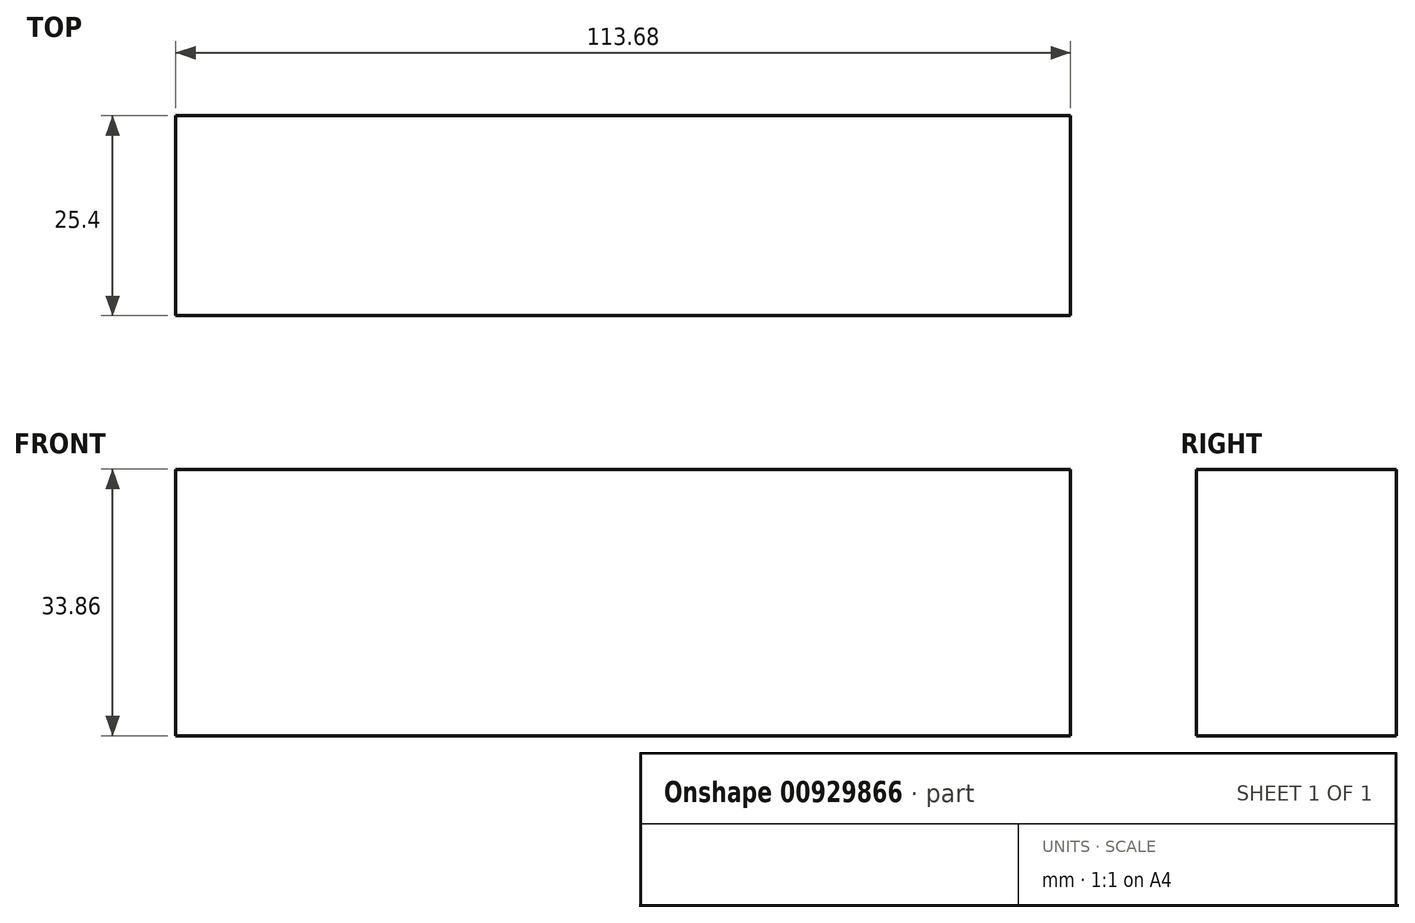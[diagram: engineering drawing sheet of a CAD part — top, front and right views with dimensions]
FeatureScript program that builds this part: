
annotation { "Feature Type Name" : "Feature", "Feature Type Description" : "" }
export const myFeature = defineFeature(function(context is Context, id is Id, definition is map)
    precondition{}
    {
        {
            var Q0;
            Q0=qCreatedBy(makeId("Front.planeOp"),FACE);
            var sketch = newSketch(context, id + "F0", { "sketchPlane" : qUnion([Q0])});
            skLineSegment(sketch, "E0.bottom", {"start": v(0, 0) * mm, "end": v(113.68, 0) * mm});
            skLineSegment(sketch, "E0.top", {"start": v(0, 33.86) * mm, "end": v(113.68, 33.86) * mm});
            skLineSegment(sketch, "E0.left", {"start": v(0, 0) * mm, "end": v(0, 33.86) * mm});
            skLineSegment(sketch, "E0.right", {"start": v(113.68, 0) * mm, "end": v(113.68, 33.86) * mm});
            skSolve(sketch);
        }
        {
            var Q0;
            Q0 = qSketchRegion(id + "F0", true);
            extrude(context, id + "F1", {"entities" : qUnion([Q0]), "depth" : 25.4 * mm, "offsetDistance" : 25.4 * mm});
        }
    });
